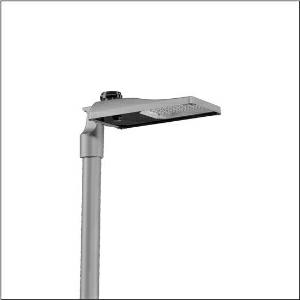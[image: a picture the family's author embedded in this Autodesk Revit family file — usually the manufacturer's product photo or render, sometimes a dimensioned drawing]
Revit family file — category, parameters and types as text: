
# Revit family: streetlight_sl_31_mini___st1_0a_5xh6d3bm08ja_37c8
name_source: partatom
category: Lighting Fixtures
units: mm (PartAtom-declared; Revit-internal decimal feet)

## family parameters
Cut with Voids When Loaded = No
Host = Face
Light Source = No
Part Type = Normal
Room Calculation Point = No
Round Connector Dimension = Use Diameter
Shared = No

## types (1)
- --- (1 x LED, 12270 lm, 82.5 W, 3000K)
    Apparent Load = 83 VA
    CIE Flux Codes = 40 73 97 100 100
    Color Rendering = 70
    Color Temperature = 3000K
    Default Elevation = 1800 mm
    Description = Streetlight SL 31 mini NEMA (7pin) mast luminaire for post-top, side-entry; light control with lens of PMMA; light distribution: ST1.0a, direct asymmetric distribution, for standard-compliant lighting for roads and squares; LED: luminous flux: 12.270lm, light colour: 730, colour temperature: 3000K; luminous efficacy: 148,7lm/W; control: pre-setting: linear dimming characteristic, flexible luminous flux parameterisation, time-dependent luminous flux control, constant luminous flux control, intelligent temperature release in ECG and LED module, overheat protection; luminaire housing, of diecast aluminium, SITECO metallic grey (DB 702S), corrosivity category C5 high according to DIN EN ISO 12944; cover of toughened safety glass, transparent, opened without tools; mast flange of diecast aluminium, SITECO metallic grey (DB 702S), spigot size: 76/60mm, mast flange included unmounted; cable length: 10,5m, connection cable pre-assembled; mains connection: 220..240V, AC, 50/60Hz; power consumption (at start of service life): 82,5W / (at end of service life): 90,1W / (with reduced operation 50%): 36,8W; protection rating (complete): IP66; insulation class (complete): insulation class I (protective earthing); impact resistance: IK09; certification: CE, ENEC, ENEC+, VDE, UKCA; permissible operating ambient temperature for outdoor applications: -40..+50°C; packaging unit: 1 piece

Light Distribution: ST1.0a
    Height = 76 mm
    Lamp = 1 x LED
    Lamp Light Flux = 12270 lm
    Lamp Power = 82.5 W
    Lamp count = 1
    Length = 547 mm
    Luminous efficacy = 149 lm/W
    Manufacturer = Siteco
    ModVariant = No
    Model = 5XH6D3BM08JA
    Number of Poles = 1
    OnlyDefault = Yes
    Power Factor = 1
    Product Name = Streetlight SL 31 mini | ST1.0a
    Product group = mast luminaire | pylon top
    ProductGroupID = 6100
    Protection Class = Protection class I
    Protection Degree = IP 66
    RLX_Detail_Level = 1
    RLX_Emergency_Light_Flux = 0 lm
    RLX_Emergency_Type = 0
    RLX_Emergency_Type_DB = No
    RlxData = <blob elided: 40269 chars, md5=7e2d2296>
    Socket = socket
    Standby Power = 0 W
    System Light Flux = 12270 lm
    System Power = 83 W
    Type Comments = factory setting: luminous flux: 100 % | dim-lin: 254 | 870 mA
    Type Image = l_1300324.jpg
    URL = http://relux.com
    VarID = @adj_056875
    Voltage = 0 V
    Weight = 0.00 kg
    Width = 265 mm

## geometry (parser evidence)
native form markers: Blend x4, Sweep x10
no freeform markers — native parametric forms only
